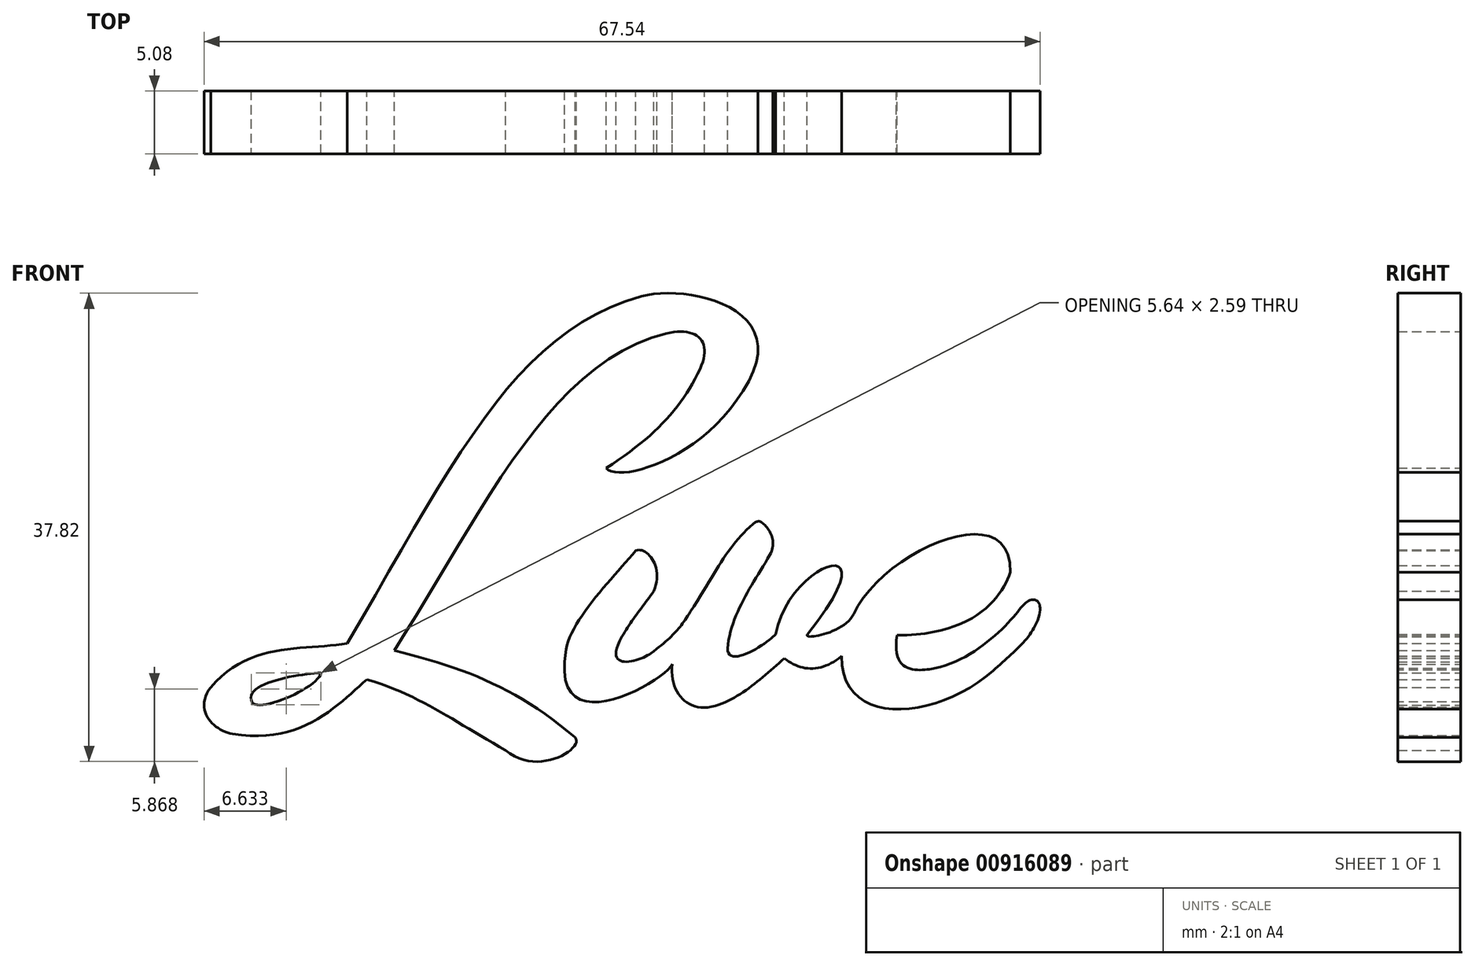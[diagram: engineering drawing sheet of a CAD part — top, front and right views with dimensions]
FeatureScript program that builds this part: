
annotation { "Feature Type Name" : "Feature", "Feature Type Description" : "" }
export const myFeature = defineFeature(function(context is Context, id is Id, definition is map)
    precondition{}
    {
        {
            var Q0;
            Q0=qCreatedBy(makeId("Front.planeOp"),FACE);
            var sketch = newSketch(context, id + "F0", { "sketchPlane" : qUnion([Q0])});
            skFitSpline(sketch, "E0", {"points": [v(-8.9, 17.7) * mm, v(2.61, 24.73) * mm], "startDerivative": vector(3.1, -3.78) * mm, "endDerivative": vector(10.11, 18.83) * mm});
            skFitSpline(sketch, "E1", {"points": [v(-6.04, 31.58) * mm, v(-29.8, 3.55) * mm], "startDerivative": vector(-30.23, -8.53) * mm, "endDerivative": vector(-27.08, -46.5) * mm});
            skFitSpline(sketch, "E2", {"points": [v(-6.04, 31.58) * mm, v(2.61, 24.73) * mm], "startDerivative": vector(10, 2.82) * mm, "endDerivative": vector(-9.96, -18.55) * mm});
            skFitSpline(sketch, "E3", {"points": [v(-4.07, 28.58) * mm, v(-26.02, 2.97) * mm], "startDerivative": vector(-28.46, -6.8) * mm, "endDerivative": vector(-20.35, -31.78) * mm});
            skFitSpline(sketch, "E4", {"points": [v(-4.07, 28.58) * mm, v(-1.32, 25.7) * mm], "startDerivative": vector(7.42, 1.77) * mm, "endDerivative": vector(-3.18, -6.8) * mm});
            skFitSpline(sketch, "E5", {"points": [v(-1.32, 25.7) * mm, v(-8.9, 17.7) * mm], "startDerivative": vector(-4.43, -9.48) * mm, "endDerivative": vector(-11.86, -7.68) * mm});
            skFitSpline(sketch, "E6", {"points": [v(-26.02, 2.97) * mm, v(-11.4, -4.04) * mm], "startDerivative": vector(16.83, -4.14) * mm, "endDerivative": vector(14.32, -12.13) * mm});
            skFitSpline(sketch, "E7", {"points": [v(-27.72, 13.35) * mm, v(-24.5, 18.85) * mm], "startDerivative": vector(11.53, 1.66) * mm, "endDerivative": vector(3.49, 5.78) * mm, "construction": true});
            skFitSpline(sketch, "E8", {"points": [v(-26.41, 12.46) * mm, v(-27.73, 12.9) * mm], "startDerivative": vector(-1.01, 0.95) * mm, "endDerivative": vector(-1.33, 0.2) * mm, "construction": true});
            skArc(sketch, "E9", {"start": v(-27.72, 13.35) * mm, "mid": v(-27.92, 13.13) * mm, "end": v(-27.73, 12.9) * mm, "construction": true});
            skFitSpline(sketch, "E10", {"points": [v(-24.5, 18.85) * mm, v(-30.54, 17.17) * mm], "startDerivative": vector(-12.3, 7.07) * mm, "endDerivative": vector(-7.12, -5.44) * mm, "construction": true});
            skFitSpline(sketch, "E11", {"points": [v(-30.54, 17.17) * mm, v(-30.33, 19.87) * mm, v(-31.21, 21.03) * mm, v(-31.44, 22.45) * mm, v(-29.97, 25.41) * mm, v(-26.54, 27.74) * mm, v(-24.16, 29.12) * mm], "startDerivative": vector(4.01, 17.75) * mm, "endDerivative": vector(12.72, 7.66) * mm, "construction": true});
            skFitSpline(sketch, "E12", {"points": [v(-24.16, 29.12) * mm, v(-27.82, 25.86) * mm], "startDerivative": vector(-0.66, -5.14) * mm, "endDerivative": vector(-4.48, -2.82) * mm, "construction": true});
            skFitSpline(sketch, "E13", {"points": [v(-27.82, 25.86) * mm, v(-30.26, 23) * mm], "startDerivative": vector(-5.31, -1.33) * mm, "endDerivative": vector(-1.33, -2) * mm});
            skFitSpline(sketch, "E14", {"points": [v(-30.26, 23) * mm, v(-24.18, 26.25) * mm], "startDerivative": vector(5.95, 2.94) * mm, "endDerivative": vector(5.95, 2.94) * mm, "construction": true});
            skFitSpline(sketch, "E15", {"points": [v(-24.18, 26.25) * mm, v(-22.3, 32.28) * mm], "startDerivative": vector(6.17, 4.25) * mm, "endDerivative": vector(-1.92, 6.03) * mm, "construction": true});
            skFitSpline(sketch, "E16", {"points": [v(-22.3, 32.28) * mm, v(-33.15, 24.13) * mm], "startDerivative": vector(-3.91, -8.73) * mm, "endDerivative": vector(0.42, -11.2) * mm});
            skFitSpline(sketch, "E17", {"points": [v(-28.23, 0.63) * mm, v(-39.08, -3.75) * mm], "startDerivative": vector(-7.04, -6.01) * mm, "endDerivative": vector(-16.9, 2.85) * mm});
            skFitSpline(sketch, "E18", {"points": [v(-29.8, 3.55) * mm, v(-40.85, 0) * mm], "startDerivative": vector(-10.2, -1.7) * mm, "endDerivative": vector(-9.6, -11.24) * mm});
            skFitSpline(sketch, "E19", {"points": [v(-39.08, -3.75) * mm, v(-40.85, 0) * mm], "startDerivative": vector(-4.59, 0.77) * mm, "endDerivative": vector(4.25, 5.64) * mm});
            skFitSpline(sketch, "E20", {"points": [v(-28.23, 0.63) * mm, v(-17.01, -5.09) * mm], "startDerivative": vector(13.37, -3.92) * mm, "endDerivative": vector(12.28, -6.79) * mm});
            skFitSpline(sketch, "E21", {"points": [v(-17.01, -5.09) * mm, v(-11.4, -4.04) * mm], "startDerivative": vector(7.9, -6.61) * mm, "endDerivative": vector(-2.43, 2.53) * mm});
            skFitSpline(sketch, "E22", {"points": [v(-31.94, 1.17) * mm, v(-37.5, -1.2) * mm], "startDerivative": vector(-5.57, -0.25) * mm, "endDerivative": vector(2.62, -4.6) * mm});
            skFitSpline(sketch, "E23", {"points": [v(-31.94, 1.17) * mm, v(-37.5, -1.2) * mm], "startDerivative": vector(-0.56, -3.52) * mm, "endDerivative": vector(-1.57, 2.75) * mm});
            skSolve(sketch);
        }
        {
            var Q0;
            Q0 = qSketchRegion(id + "F0", true);
            extrude(context, id + "F1", {"entities" : qUnion([Q0]), "depth" : 5.08 * mm, "offsetDistance" : 25.4 * mm});
        }
        {
            var Q0;
            Q0=qCreatedBy(makeId("Front.planeOp"),FACE);
            var sketch = newSketch(context, id + "F2", { "sketchPlane" : qUnion([Q0])});
            skFitSpline(sketch, "E24", {"points": [v(-6.53, 11.03) * mm, v(-12.14, 3.07) * mm], "startDerivative": vector(-5.72, -6.78) * mm, "endDerivative": vector(-1.27, -7.14) * mm});
            skFitSpline(sketch, "E25", {"points": [v(-12.14, 3.07) * mm, v(-3.56, 1.86) * mm], "startDerivative": vector(-4.27, -23.97) * mm, "endDerivative": vector(1.86, 3.99) * mm});
            skFitSpline(sketch, "E26", {"points": [v(-6.53, 11.03) * mm, v(-5.07, 7.76) * mm], "startDerivative": vector(2.8, 1.2) * mm, "endDerivative": vector(-2.53, -5.85) * mm});
            skFitSpline(sketch, "E27", {"points": [v(-5.07, 7.76) * mm, v(-7.81, 3.73) * mm], "startDerivative": vector(-2.75, -4.03) * mm, "endDerivative": vector(-2.17, -4.37) * mm});
            skFitSpline(sketch, "E28", {"points": [v(-7.81, 3.73) * mm, v(-5.29, 2.76) * mm], "startDerivative": vector(-3.67, -7.4) * mm, "endDerivative": vector(2.63, 1.97) * mm});
            skFitSpline(sketch, "E29", {"points": [v(-5.29, 2.76) * mm, v(-2.1, 6.1) * mm], "startDerivative": vector(5.41, 4.07) * mm, "endDerivative": vector(2.63, 4.08) * mm});
            skFitSpline(sketch, "E30", {"points": [v(-2.1, 6.1) * mm, v(2.97, 13.2) * mm], "startDerivative": vector(6.62, 10.3) * mm, "endDerivative": vector(6.28, 5.52) * mm});
            skFitSpline(sketch, "E31", {"points": [v(4.32, 10.7) * mm, v(3.6, 13.36) * mm], "startDerivative": vector(2, 3.46) * mm, "endDerivative": vector(-1.82, 1.2) * mm});
            skFitSpline(sketch, "E32", {"points": [v(3.6, 13.36) * mm, v(2.97, 13.2) * mm], "startDerivative": vector(-0.58, 0.39) * mm, "endDerivative": vector(-0.52, -0.46) * mm});
            skFitSpline(sketch, "E33", {"points": [v(-3.56, 1.86) * mm, v(0.19, -1.4) * mm], "startDerivative": vector(-0.75, -7.24) * mm, "endDerivative": vector(7.1, 2.55) * mm});
            skFitSpline(sketch, "E34", {"points": [v(0.19, -1.4) * mm, v(5.5, 2.35) * mm], "startDerivative": vector(6, 2.15) * mm, "endDerivative": vector(5.04, 4.38) * mm});
            skFitSpline(sketch, "E35", {"points": [v(5.5, 2.35) * mm, v(10.1, 2.52) * mm], "startDerivative": vector(3.84, -3.31) * mm, "endDerivative": vector(4.72, 3.98) * mm});
            skFitSpline(sketch, "E36", {"points": [v(10.1, 2.52) * mm, v(22.34, 1.34) * mm], "startDerivative": vector(-0.1, -17.8) * mm, "endDerivative": vector(13.05, 11.74) * mm});
            skFitSpline(sketch, "E37", {"points": [v(22.34, 1.34) * mm, v(25.84, 5.16) * mm], "startDerivative": vector(4.45, 4) * mm, "endDerivative": vector(1.97, 4.4) * mm});
            skFitSpline(sketch, "E38", {"points": [v(17.65, 1.55) * mm, v(24.61, 6.43) * mm], "startDerivative": vector(9.92, 1.98) * mm, "endDerivative": vector(2.64, 3.55) * mm});
            skFitSpline(sketch, "E39", {"points": [v(17.65, 1.55) * mm, v(14.6, 4.2) * mm], "startDerivative": vector(-2.88, -0.57) * mm, "endDerivative": vector(1.83, 10.13) * mm});
            skFitSpline(sketch, "E40", {"points": [v(24.61, 6.43) * mm, v(25.84, 5.16) * mm], "startDerivative": vector(2.64, 3.54) * mm, "endDerivative": vector(-2.7, -6.03) * mm});
            skFitSpline(sketch, "E41", {"points": [v(14.6, 4.2) * mm, v(23.73, 9.3) * mm], "startDerivative": vector(18.63, 0.07) * mm, "endDerivative": vector(2.05, 6.3) * mm});
            skFitSpline(sketch, "E42", {"points": [v(11.1, 5.92) * mm, v(23.73, 9.3) * mm], "startDerivative": vector(6.86, 15.13) * mm, "endDerivative": vector(-0.61, -19.04) * mm});
            skFitSpline(sketch, "E43", {"points": [v(4.32, 10.7) * mm, v(0.93, 3.44) * mm], "startDerivative": vector(-4.26, -7.33) * mm, "endDerivative": vector(-1.26, -8.32) * mm});
            skFitSpline(sketch, "E44", {"points": [v(0.93, 3.44) * mm, v(4.77, 4.28) * mm], "startDerivative": vector(-1.05, -6.95) * mm, "endDerivative": vector(1.48, 1.85) * mm});
            skFitSpline(sketch, "E45", {"points": [v(4.77, 4.28) * mm, v(7.36, 4.28) * mm], "startDerivative": vector(3.4, 17.6) * mm, "endDerivative": vector(-21.13, -26.37) * mm});
            skFitSpline(sketch, "E46", {"points": [v(7.36, 4.28) * mm, v(11.1, 5.92) * mm], "startDerivative": vector(-1.25, -1.56) * mm, "endDerivative": vector(2.1, 4.6) * mm});
            skSolve(sketch);
        }
        {
            var Q0;
            Q0 = qSketchRegion(id + "F2", true);
            var Q1;
            Q1=makeQuery(id+"F1.opExtrude","CAP_FACE",FACE,{"disambiguationData":[OSD([sQuery(id+"F0.wireOp",EDGE,"E0"),sQuery(id+"F0.wireOp",EDGE,"E1"),sQuery(id+"F0.wireOp",EDGE,"E2"),sQuery(id+"F0.wireOp",EDGE,"E3"),sQuery(id+"F0.wireOp",EDGE,"E4"),sQuery(id+"F0.wireOp",EDGE,"E5"),sQuery(id+"F0.wireOp",EDGE,"E6"),sQuery(id+"F0.wireOp",EDGE,"E17"),sQuery(id+"F0.wireOp",EDGE,"E18"),sQuery(id+"F0.wireOp",EDGE,"E19"),sQuery(id+"F0.wireOp",EDGE,"E20"),sQuery(id+"F0.wireOp",EDGE,"E21"),sQuery(id+"F0.wireOp",EDGE,"E22"),sQuery(id+"F0.wireOp",EDGE,"E23")])],"isStart":false});
            extrude(context, id + "F3", {"entities" : qUnion([Q0]), "endBound" : BoundingType.UP_TO_SURFACE, "depth" : 25.4 * mm, "endBoundEntityFace" : qUnion([Q1]), "offsetDistance" : 25.4 * mm});
        }
    });
